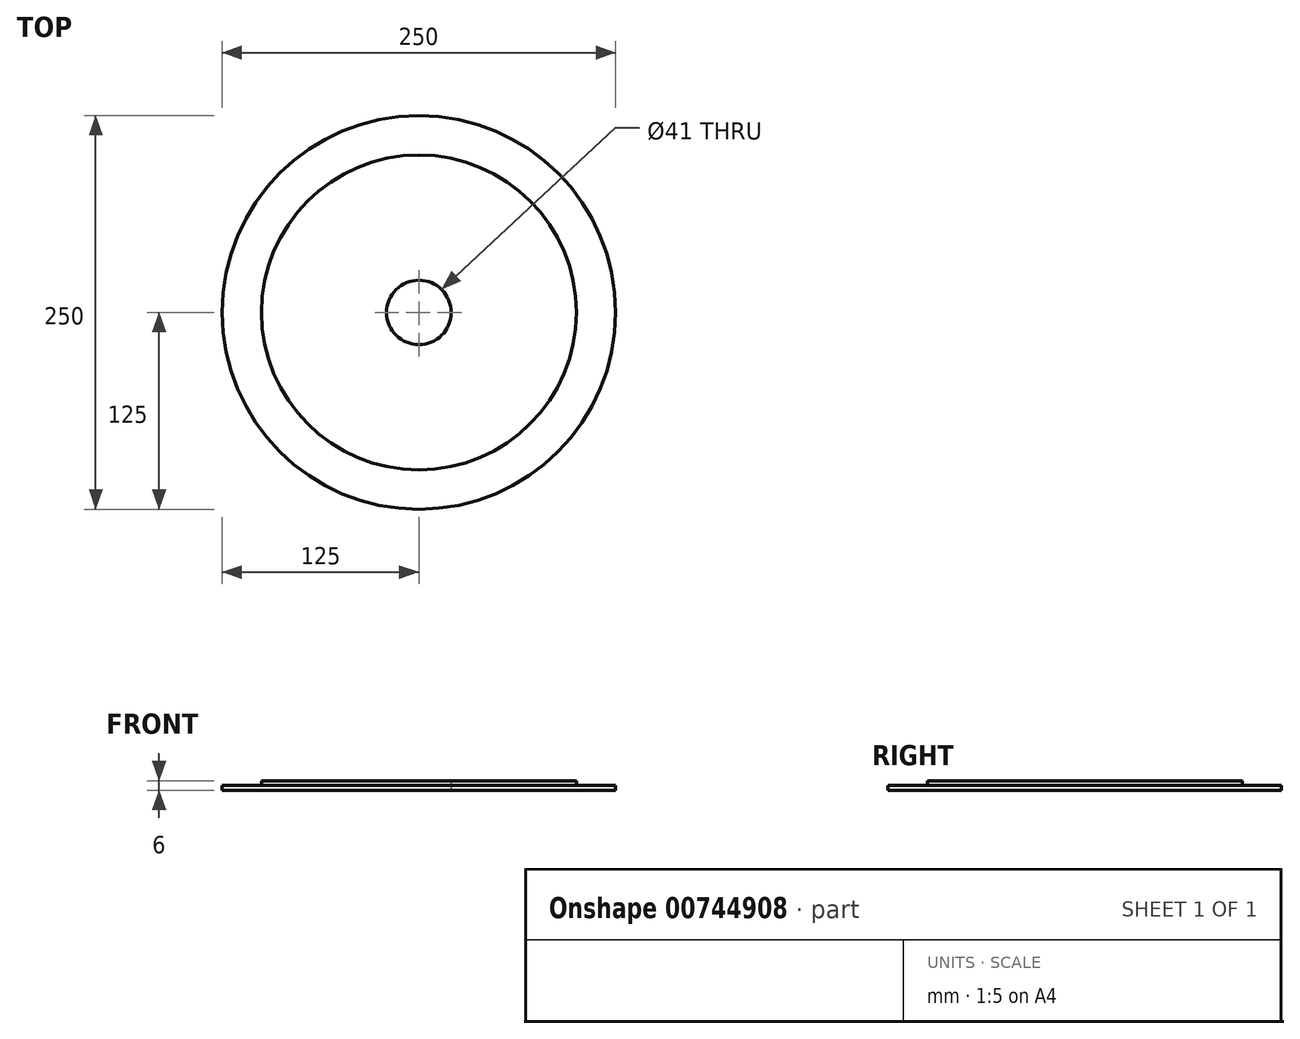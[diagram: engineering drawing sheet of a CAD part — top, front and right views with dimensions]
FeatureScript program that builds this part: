
annotation { "Feature Type Name" : "Feature", "Feature Type Description" : "" }
export const myFeature = defineFeature(function(context is Context, id is Id, definition is map)
    precondition{}
    {
        {
            var Q0;
            Q0=qCreatedBy(makeId("Top.planeOp"),FACE);
            var sketch = newSketch(context, id + "F0", { "sketchPlane" : qUnion([Q0])});
            skCircle(sketch, "E0", {"center": v(0, 0) * mm, "radius": 20.5 * mm});
            skCircle(sketch, "E1", {"center": v(0, 0) * mm, "radius": 100 * mm});
            skSolve(sketch);
        }
        {
            var Q0;
            Q0=makeQuery(id+"F0.imprint","IMPRINT",FACE,{"disambiguationData":[TD([[makeQuery(id+"F0.imprint","IMPRINT",EDGE,{"derivedFrom":sQuery(id+"F0.wireOp",EDGE,"E0")}),-1.0]])]});
            extrude(context, id + "F1", {"entities" : qUnion([Q0]), "depth" : 3 * mm, "offsetDistance" : 25 * mm});
        }
        {
            var Q0;
            Q0=qCreatedBy(makeId("Top.planeOp"),FACE);
            var sketch = newSketch(context, id + "F2", { "sketchPlane" : qUnion([Q0])});
            skCircle(sketch, "E2", {"center": v(0, 0) * mm, "radius": 45 * mm});
            skCircle(sketch, "E3", {"center": v(0, 0) * mm, "radius": 125 * mm});
            skSolve(sketch);
        }
        {
            var Q0;
            Q0 = qSketchRegion(id + "F2", true);
            var Q1;
            Q1=makeQuery(id+"F1.opExtrude","CAP_FACE",FACE,{"disambiguationData":[OSD([sQuery(id+"F0.wireOp",EDGE,"E0"),sQuery(id+"F0.wireOp",EDGE,"E1")])],"isStart":false});
            extrude(context, id + "F3", {"entities" : qUnion([Q0, Q1]), "operationType" : NewBodyOperationType.ADD, "depth" : 3 * mm, "offsetDistance" : 25 * mm});
        }
    });
